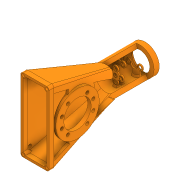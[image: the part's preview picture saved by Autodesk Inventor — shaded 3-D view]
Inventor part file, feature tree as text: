
AUTODESK INVENTOR PART (.ipt)
format: ipt  version: 2020 (Build 240168000, 168)  size: 1,342,976 bytes
history: native  units: in
note: dims shown in document units (in); Inventor stores cm internally (conversion verified against a paired STEP export)
features: sketch x25, chamfer x24, extrude x22, projected_geometry x12, plane x3, loft x2, fillet x1, other x1
ambient origin geometry x8: Origin, YZ Plane, XZ Plane, XY Plane, X Axis, Y Axis, Z Axis, Center Point
bodies: Solid1 (feature_tree)
feature tree (90):
  extrude  "Extrusion1"  Depth=2.0472in
  extrude  "Extrusion2"  Depth=1.6535in
  chamfer  "Chamfer1"  Distance=0.5512in
  extrude  "Extrusion3"  Depth=0.0157in
  extrude  "Extrusion4"  Depth=0.2756in TaperAngle=0.0deg
  extrude  "Extrusion5"  Depth=0.315in
  extrude  "Extrusion6"  Depth=0.4724in
  extrude  "Extrusion7"  Depth=0.0787in
  plane  "Work Plane1"
  extrude  "Extrusion8"  Depth=0.1575in
  plane  "Work Plane2"
  extrude  "Extrusion9"  Depth=1.0994in
  sketch  "Sketch11"  dims[d31=15.0deg d32=0.4921in d33=0.0in]
  plane  "Work Plane3"
  extrude  "Extrusion10"  Depth=0.4921in TaperAngle=0.0deg
  extrude  "Extrusion11"  Depth=1.5748in TaperAngle=360.0deg
  loft  "Loft1"
  loft  "Loft2"
  sketch  "Sketch16"  dims[d47=0.315in d48=0.4331in]
  extrude  "Extrusion12"  Depth=0.0984in TaperAngle=0.0deg
  extrude  "Extrusion13"  Depth=0.4331in
  extrude  "Extrusion14"  Depth=0.6161in
  extrude  "Extrusion15"  Depth=0.1575in
  chamfer  "Chamfer2"  Distance=0.0984in
  chamfer  "Chamfer3"  Distance=0.1969in
  chamfer  "Chamfer4"  Distance=0.1969in
  chamfer  "Chamfer5"  Distance=0.3484in
  chamfer  "Chamfer6"  Distance=0.3484in
  chamfer  "Chamfer7"  Distance=0.1969in
  chamfer  "Chamfer8"  Distance=0.1969in
  chamfer  "Chamfer9"  Distance=0.1969in
  chamfer  "Chamfer10"  Distance=0.3937in
  chamfer  "Chamfer11"  Distance=0.7874in
  chamfer  "Chamfer12"  Angle=90.0deg  [1 undecoded]
  chamfer  "Chamfer13"  Angle=90.0deg  [1 undecoded]
  chamfer  "Chamfer14"  Angle=90.0deg  [1 undecoded]
  chamfer  "Chamfer15"  Angle=90.0deg  [1 undecoded]
  chamfer  "Chamfer16"  Distance=0.7874in
  chamfer  "Chamfer17"  Distance=0.3937in
  chamfer  "Chamfer18"  Distance=0.3937in
  chamfer  "Chamfer19"  Distance=0.7874in
  chamfer  "Chamfer20"  Distance=0.1969in
  chamfer  "Chamfer21"  Distance=0.8858in
  chamfer  "Chamfer22"  Distance=1.6654in
  fillet  "Fillet1"  Radius=1.6654in
  chamfer  "Chamfer23"  [1 undecoded]
  extrude  "Extrusion19"  TaperAngle=0.0deg  [1 undecoded]
  extrude  "Extrusion20"  Depth=0.2224in
  extrude  "Extrusion21"  Depth=0.1575in
  extrude  "Extrusion22"  Depth=0.1575in
  extrude  "Extrusion23"  Depth=0.1575in
  extrude  "Extrusion24"  Depth=0.1575in
  extrude  "Extrusion25"  Depth=0.0984in
  chamfer  "Chamfer24"  Distance=0.0984in
  sketch  "Sketch1"  dims[d0=2.3622in d1=2.0472in]
  sketch  "Sketch2"  dims[d2=0.2756in d3=0.0in d4=1.6535in d5=0.5512in d6=0.0in]
  sketch  "Sketch3"  dims[d7=0.2756in d8=0.125in d9=0.0137in d10=0.0157in]
  sketch  "Sketch5"  dims[d11=4.7244in d13=360.0deg d15=0.2756in d16=0.0in]
  sketch  "Sketch6"  dims[d17=0.5512in d19=0.315in]
  projected_geometry  "Projected Loop1"
  sketch  "Sketch7"  dims[d20=0.315in d21=0.4724in]
  projected_geometry  "Projected Loop2"
  sketch  "Sketch8"  dims[d22=0.4724in d23=0.0787in d24=0.0787in d25=0.0787in]
  projected_geometry  "Projected Loop3"
  sketch  "Sketch9"  dims[d26=0.0984in d27=0.0in d28=0.1575in]
  sketch  "Sketch10"  dims[d29=0.1575in d30=1.0994in]
  sketch  "Sketch12"  dims[d34=1.4567in d35=0.0in d36=1.5748in d38=360.0deg]
  sketch  "Sketch13"  dims[d40=0.0787in d41=0.0787in]
  projected_geometry  "Projected Loop4"
  other  "Edges1"
  sketch  "Sketch14"  dims[d42=0.0787in d43=0.0787in]
  projected_geometry  "Projected Loop5"
  sketch  "Sketch15"  dims[d44=0.0787in d45=0.0984in d46=0.0in]
  projected_geometry  "Projected Loop6"
  projected_geometry  "Projected Loop7"
  sketch  "Sketch19"  dims[d49=0.0984in d50=0.0in d51=0.6161in]
  projected_geometry  "Projected Loop8"
  sketch  "Sketch20"  dims[d52=0.1575in d53=0.1575in d54=0.0984in d55=0.0in]
  projected_geometry  "Projected Loop9"
  sketch  "Sketch21"  dims[d56=6.6929in]
  sketch  "Sketch25"  dims[d57=0.8858in]
  sketch  "Sketch26"  dims[d58=1.6654in]
  projected_geometry  "Projected Loop11"
  sketch  "Sketch27"  dims[d59=1.6654in]
  projected_geometry  "Projected Loop12"
  sketch  "Sketch28"  dims[d60=0.0in]
  sketch  "Sketch29"  dims[d61=0.0in]
  sketch  "Sketch30"  dims[d62=1.6654in]
  sketch  "Sketch31"  dims[d63=1.6654in d64=0.1969in d65=0.1969in d66=0.3484in d67=0.3484in d68=0.1969in d69=0.1969in d70=0.1969in d71=0.3937in d72=0.0in d73=0.7874in d74=0.0in d75=0.0in d76=90.0deg d77=0.0in d78=90.0deg d79=0.0in d80=90.0deg d81=0.0in d82=90.0deg d86=0.7874in d87=0.0in d90=0.3937in d91=0.3937in d92=0.7874in d93=0.0in d94=0.1969in d95=0.0in d96=0.8858in d97=1.6654in d98=1.6654in d99=0.0in d100=0.0in d101=0.2224in d102=0.1575in d103=0.1575in d104=0.1575in d105=0.1575in d106=0.0984in d107=0.0984in d108=0.1969in d109=0.0in d122=0.1575in d123=0.0787in d124=45.0deg d125=0.0787in d126=0.1575in d127=45.0deg d128=0.1575in d129=0.0787in d130=45.0deg d131=0.0787in d132=0.1575in d133=45.0deg d134=0.1575in d135=0.0787in d136=45.0deg d137=0.1575in d138=0.0787in d139=45.0deg d140=0.1575in d141=0.0787in d142=45.0deg d143=0.1575in d144=0.0787in d145=45.0deg d146=0.0787in d147=0.1575in d148=45.0deg d149=0.1575in d150=0.0787in d151=45.0deg d152=0.1575in d153=0.0787in d154=45.0deg d155=0.0787in d156=0.1575in d157=45.0deg d158=0.0591in d159=0.1575in d160=0.0137in d161=0.0591in d162=0.1575in d163=0.0137in d164=0.0591in d165=0.1575in d166=0.0137in d167=0.0591in d168=0.1575in d169=0.0137in d170=0.0591in d171=0.1575in d172=0.0137in d173=0.0591in d174=0.1575in d175=0.0137in d176=0.0591in d177=0.1575in d178=0.0137in d179=0.0591in d180=0.1575in d181=0.0137in d182=0.0591in d183=0.1575in d184=0.0137in d185=0.0118in d193=0.0984in d194=0.3937in d195=0.125in d196=45.0deg d197=0.2756in d198=0.1969in d199=0.0in d200=0.2756in d201=2.7559in d202=0.2756in d203=0.2756in d204=0.2756in d205=0.2756in d206=0.2756in d207=0.2756in d208=0.2756in d209=0.0394in d210=0.2047in d211=0.0in d212=0.1969in d213=0.2756in d214=0.0in d215=1.0in d216=0.0in d217=0.2362in d218=0.2362in d219=0.2362in d220=0.2362in d221=0.2362in d222=0.0in d223=0.3937in d224=0.0in d225=0.1575in d226=0.0in d227=0.315in d228=0.187in d229=0.125in d230=45.0deg]
  projected_geometry  "Projected Loop13"
note: 6 required parameter values undecoded (feature->parameter linkage not recoverable at this tier; creation-order binding heuristic only, values carry confidence <= 0.55)
